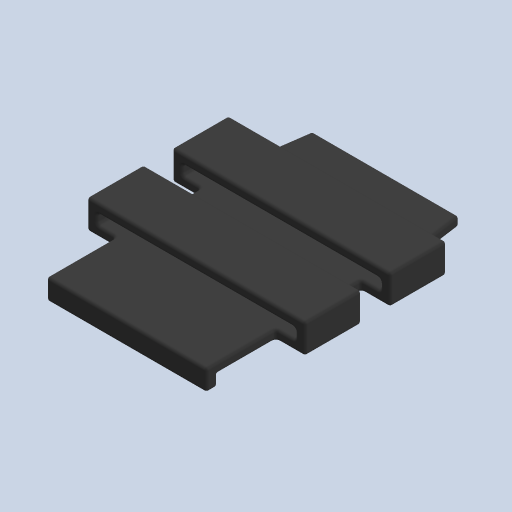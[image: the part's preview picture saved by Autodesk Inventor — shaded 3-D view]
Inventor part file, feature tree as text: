
AUTODESK INVENTOR PART (.ipt)
format: ipt  version: 2023 (Build 270158000, 158)  size: 610,304 bytes
history: native  units: mm
features: other x9, extrude x6, fillet x2, pattern_linear x1, plane x1, sketch x1
ambient origin geometry x8: Origin, YZ Plane, XZ Plane, XY Plane, X Axis, Y Axis, Z Axis, Center Point
bodies: Solid1 (feature_tree)
feature tree (20):
  other  "NP1_Payload.ipt"
  other  "Sk:Base"
  other  "Sk:Params"
  extrude  "Ex:Base"  Depth=0.7mm TaperAngle=0.0deg
  extrude  "Ex:EndLip"  Depth=0.5mm TaperAngle=0.0deg
  other  "EndPlane"
  other  "Sk:Slot"
  extrude  "Ex:Slot1"  Depth=0.7mm
  extrude  "Ex:SlotEnd"  Depth=0.7mm
  extrude  "Ex:TaperSection"  Depth=0.7mm
  pattern_linear  "Pat:Slot2"  Spacing1=0.2mm  [1 undecoded]
  plane  "Work Plane5"
  fillet  "Fillet:ExcludeLine1"  Radius=4.0mm
  extrude  "Ex:InsideStorage"  Depth=0.7mm TaperAngle=0.0deg
  fillet  "Fillet:Final"  Radius=1.0mm
  other  "TaggingFeature1"
  sketch  "Sketch3"  dims[d0=10.0mm d5=0.7mm d6=0.0mm d50=0.8mm d51=0.0mm d54=0.7mm d55=0.7mm d56=0.7mm d58=0.2mm d59=4.0mm d60=0.0mm d61=0.7mm d62=0.0mm d63=1.0mm d64=3.0mm d65=0.25mm d66=1.0mm d67=3.0mm d68=0.25mm d72=0.7mm d73=0.0mm d77=1.0mm d79=0.0mm d80=0.0mm d81=0.0mm d93=20.0mm d95=6.0mm d96=1.0mm d118=0.2mm d119=0.2mm d130=2.0mm d131=0.0mm d132=1.7mm d133=0.25mm d134=0.25mm d135=0.7mm d136=0.7mm d137=0.7mm d138=0.2mm d139=5.0mm d140=0.0mm d141=0.02mm d144=6.7mm d148=0.7mm d149=0.2mm d150=0.2mm d151=0.2mm d152=0.2mm d153=0.7mm d154=14.0mm d155=7.0mm d176=2.0mm d177=2.0mm d178=2.0mm d179=2.0mm d192=2.0mm d196=2.8mm d199=2.0mm d200=0.2mm d22=0.5mm d23=0.872665mm d24=0.5mm d25=0.872665mm d40=0.5mm d41=0.872665mm d42=0.5mm d43=0.872665mm d94=0.872665mm d116=0.5mm d117=0.872665mm d128=0.5mm d129=0.872665mm d145=0.872665mm d146=0.5mm d147=0.872665mm d158=0.5mm d159=0.872665mm d160=0.5mm d161=0.872665mm d163=0.0mm d164=0.0mm d165=0.0mm d166=0.0mm d181=0.0mm d182=0.0mm d183=0.0mm d184=0.0mm d185=0.0mm d186=0.0mm d187=0.0mm d188=0.0mm d191=0.5mm d193=0.5mm d194=0.872665mm d197=0.0mm d198=0.0mm]
  other  "Sk:InsideStorage"
  other  "Solid1::NP1_Payload.ipt"
  other  "Srf1"
note: 1 required parameter value undecoded (feature->parameter linkage not recoverable at this tier; creation-order binding heuristic only, values carry confidence <= 0.55)
